# Revit family: Seating-Teknion-Amicus-NAMGD_Amicus Gust
name_source: partatom
category: Furniture
units: mm (PartAtom-declared; Revit-internal decimal feet)

## family parameters
Always vertical = Yes
Cut with Voids When Loaded = No
OmniClass Number = 23.40.20.00
OmniClass Title = General Furniture and Specialties
Room Calculation Point = No
Shared = Yes
Work Plane-Based = No

## types (3) — shared parameters
Assembly Code = E2020200
Manufacturer = Teknion
Manufacturer Fax = 416.661.4586
Part Number = NAMGD
Product Documentation Link = https://www.teknion.com
Product Line = Amicus
Product Page URL = https://www.teknion.com
Series = Seating
Sustainability Data = https://www.teknion.com
URL = www.teknion.com
Unit Weight URL = http://www.teknion.com
Warranty = http://www.teknion.com
zero-valued in all types: Default Elevation

## per-type parameters (varying)
| type | Description | Four Leg w/ Caster Style | Four leg Styple | Model |
| Cantilever | Amicus Work Chair, Cantilever | No | No | NAMGDC_ |
| Four Leg | Amicus Work Chair, Four Leg | No | Yes | NAMGDF_ |
| Four Leg w/Casters | Amicus Work Chair, Four Leg w/Casters | Yes | No | NAMGDG_ |

type visibility flags (boolean, named after types; folded from table):
- Cantilever: Yes: Cantilever Style
- Four Leg: Yes: (none)
- Four Leg w/Casters: Yes: (none)

## geometry (parser evidence)
native form markers: Sweep x3
no freeform markers — native parametric forms only
